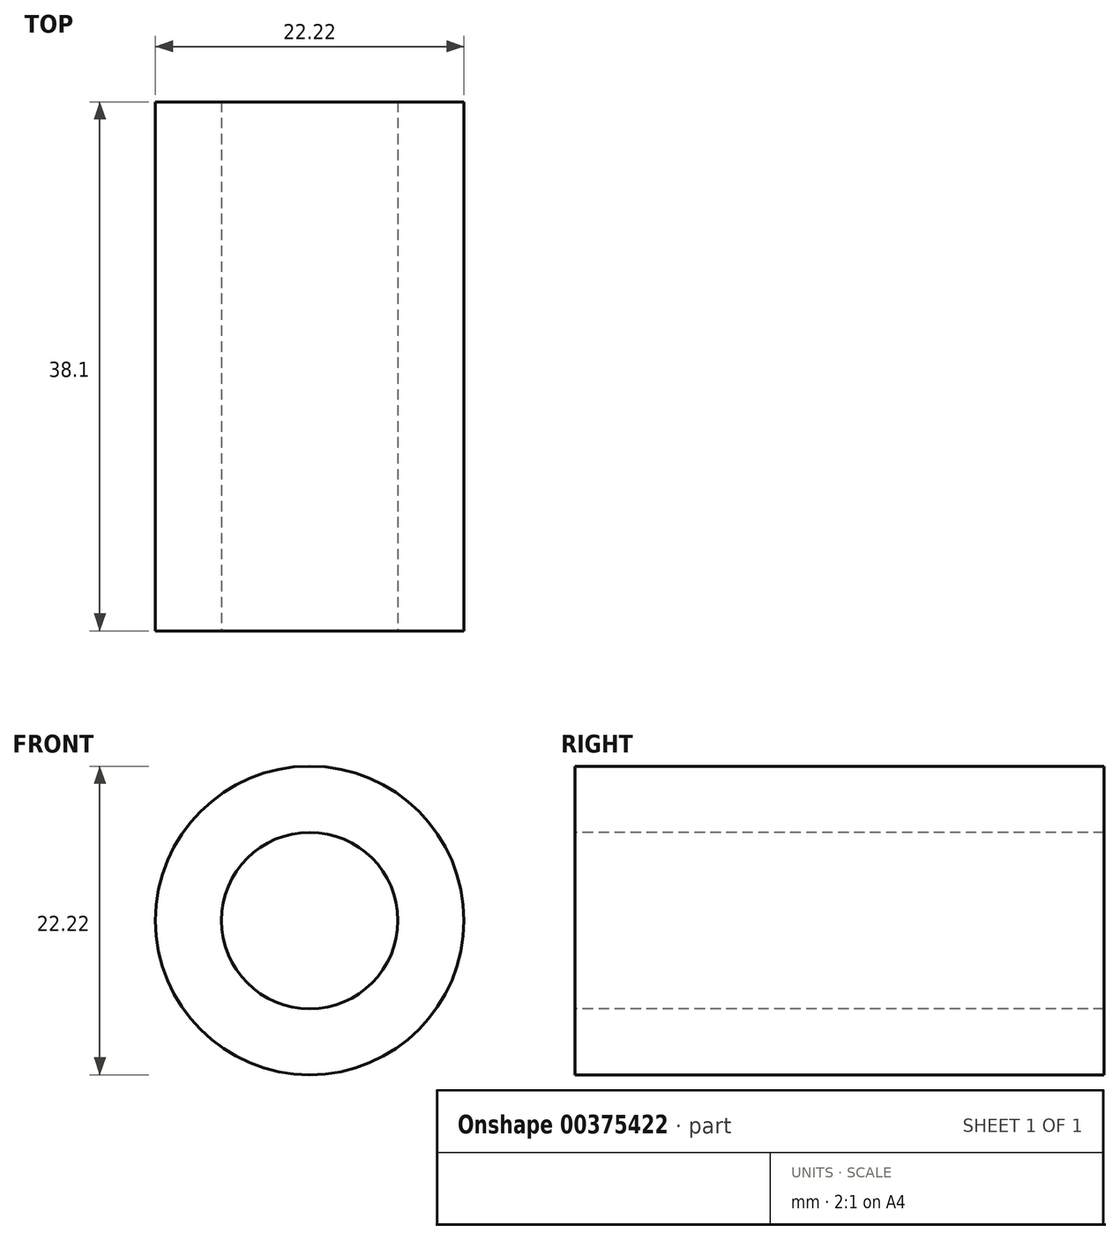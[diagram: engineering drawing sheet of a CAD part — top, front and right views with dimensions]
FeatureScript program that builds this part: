
annotation { "Feature Type Name" : "Feature", "Feature Type Description" : "" }
export const myFeature = defineFeature(function(context is Context, id is Id, definition is map)
    precondition{}
    {
        {
            var Q0;
            Q0=qCreatedBy(makeId("Front.planeOp"),FACE);
            var sketch = newSketch(context, id + "F0", { "sketchPlane" : qUnion([Q0])});
            skCircle(sketch, "E0", {"center": v(0, 0) * mm, "radius": 11.11 * mm});
            skSolve(sketch);
        }
        {
            var Q0;
            Q0=qSketchRegion(id+"F0",true);
            extrude(context, id + "F1", {"entities" : qUnion([Q0]), "depth" : 38.1 * mm, "symmetric" : true});
        }
        {
            var Q0;
            Q0=makeQuery(id+"F1.opExtrude","CAP_FACE",FACE,{"disambiguationData":[OSD([sQuery(id+"F0.wireOp",EDGE,"E0")])],"isStart":false});
            var sketch = newSketch(context, id + "F2", { "sketchPlane" : qUnion([Q0])});
            skCircle(sketch, "E1", {"center": v(0, 0) * mm, "radius": 6.35 * mm});
            skSolve(sketch);
        }
        {
            var Q0;
            Q0=makeQuery(id+"F2.imprint","IMPRINT",FACE,{"disambiguationData":[TD([[makeQuery(id+"F2.imprint","IMPRINT",EDGE,{"derivedFrom":sQuery(id+"F2.wireOp",EDGE,"E1")}),1.0]])]});
            extrude(context, id + "F3", {"entities" : qUnion([Q0]), "operationType" : NewBodyOperationType.REMOVE, "endBound" : BoundingType.THROUGH_ALL, "oppositeDirection" : true, "depth" : 25.4 * mm});
        }
    });
